# Revit family: M300
name_source: partatom
category: 衛工裝置
revit_build: Autodesk Revit 2018 (Build: 20170223_1515(x64)
units: mm (PartAtom-declared; Revit-internal decimal feet)

## family parameters
OmniClass 標題 = Other Sanitary Washing Plumbing Fixtures
OmniClass 編號 = 23.45.05.14.99
以工作平面為基礎 = 是
共用 = 是
圓形接點標註 = 使用半徑
房間計算點 = 否
組件類型 = 正常
總是垂直 = 否
載入時使用空心切割 = 否

## types (3) — shared parameters
ADA Compliant = 是
Buy American Act Compliant = 是
CW 接頭 = 是
CWFU = 10
Finish(es) = CP, PVDSF, PVDPB, PVDBN
Fixture Color = Not Applicable
Flush Choice = Single Flush
HW 接頭 = 否
IAPMO Certification = cUPC
Inlet Spud Radius = 1/2"
Inlet Spud Size = 1" IPS
Mounting = Exposed
Operation = Manual
Price = Prices may vary. Please consult Sloan Rep for most up-to-date price list.
Product Page URL = http://www.sloanvalve.com
Revision Date = 12/6/2015
Rough In = 11-1/2"
Spud Location = Top Spud
URL = www.sloanvalve.com
WFU = 10
Warranty = 3 Year (Limited)
廢水口接頭 = 否
描述 = Exposed Water Closet Flushometer for floor mounted or wall hung top spud bowls.
組合代碼 = D2020300
製造商 = SLOAN
通風口接頭 = 否
預設高程 = 0"
zero-valued in all types: HWFU

## per-type parameters (varying)
| type | Flush Volume | 模型 |
| Sloan 111-1.28 | 1.28 gpf (4.8 Lpf) | Royal 111-1.28 |
| Sloan 111-1.6 | 1.6 gpf (6.0 Lpf) | Royal 111-1.6 |
| Sloan 110- 3.5 | 3.5 gpf (13.2 Lpf) | Royal 111-1.6 |

## geometry (parser evidence)
native form markers: Sweep x1
no freeform markers — native parametric forms only
